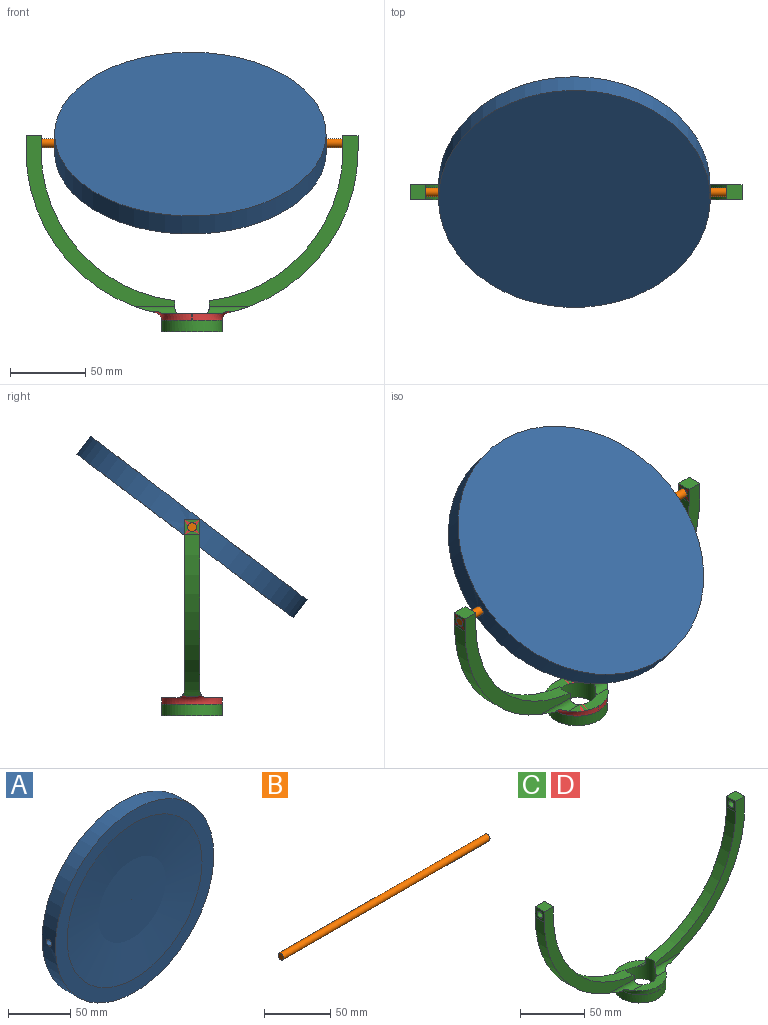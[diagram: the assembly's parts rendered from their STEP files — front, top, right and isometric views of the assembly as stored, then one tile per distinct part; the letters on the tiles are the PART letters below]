
ASSEMBLY  parts=4 mates=2
PART A: 5 faces, bbox 180x20.2x180 mm
  f0: cylinder r=90mm len=180mm, axis (0,1,0), area 8425mm2, adj f1,f2,f3
  f1: plane 180x180mm, normal (0,-1,0), area 7010.2mm2, adj f0,f4
  f2: plane 180x180mm, normal (0,1,0), area 25446.9mm2, adj f0
  f3: cylinder r=3mm len=180mm, axis (-1,0,0), area 3392mm2, adj f0
  f4: torus R=16.77mm, axis (0,1,0), area 18487.8mm2, adj f1
PART B: 3 faces, bbox 220x5.9x5.9 mm
  f0: cylinder r=2.95mm len=220mm, axis (-1,0,0), area 4077.8mm2, adj f1,f2
  f1: plane 5.9x5.9mm, normal (1,0,0), area 27.3mm2, adj f0
  f2: plane 5.9x5.9mm, normal (-1,0,0), area 27.3mm2, adj f0
PART C: 29 faces, bbox 220x40x130 mm
  f0: plane 113.17x98.54mm, normal (0,-1,0), area 1535.6mm2, adj f4,f5,f6,f12,f13,f21,f25
  f1: cylinder r=100mm len=99.34mm, axis (0,1,0), area 1448.9mm2, adj f3,f11,f14,f21
  f2: plane 113.17x98.54mm, normal (0,1,0), area 1535.6mm2, adj f4,f5,f6,f12,f13,f21,f23
  f3: plane 113.17x98.54mm, normal (0,-1,0), area 1535.6mm2, adj f1,f8,f9,f10,f11,f21,f22
  f4: plane 10x10mm, normal (0,0,1), area 100mm2, adj f0,f2,f5,f13
  f5: plane 10x10mm, normal (-1,0,0), area 71.7mm2, adj f0,f2,f4,f6,f15
  f6: cylinder r=110mm len=107.37mm, axis (0,1,0), area 1485.5mm2, adj f0,f2,f5,f23,f25,f26
  f7: plane 40x40mm, normal (0,0,-1), area 765.8mm2, adj f21,f27
  f8: cylinder r=110mm len=107.37mm, axis (0,1,0), area 1485.5mm2, adj f3,f9,f14,f22,f24,f28
  f9: plane 10x10mm, normal (1,0,0), area 71.7mm2, adj f3,f8,f10,f14,f16
  f10: plane 10x10mm, normal (0,0,1), area 100mm2, adj f3,f9,f11,f14
  f11: plane 10x10mm, normal (-1,0,0), area 71.7mm2, adj f1,f3,f10,f14,f16
  f12: cylinder r=100mm len=99.34mm, axis (0,1,0), area 1448.9mm2, adj f0,f2,f13,f21
  f13: plane 10x10mm, normal (1,0,0), area 71.7mm2, adj f0,f2,f4,f12,f15
  f14: plane 113.17x98.54mm, normal (0,1,0), area 1535.6mm2, adj f1,f8,f9,f10,f11,f21,f24
  f15: cylinder r=3mm len=10mm, axis (1,0,0), area 188.5mm2, adj f5,f13
  f16: cylinder r=3mm len=10mm, axis (1,0,0), area 188.5mm2, adj f9,f11
  f17: plane 36.99x10mm, normal (0,0,1), area 235.1mm2, adj f18,f21,f22,f25,f26,f28
  f18: plane 4.08x0.67mm, normal (0,-1,0), area 0.9mm2, adj f17,f26,f28
  f19: plane 36.99x10mm, normal (0,0,1), area 235.1mm2, adj f20,f21,f23,f24,f26,f28
  f20: plane 4.08x0.67mm, normal (0,1,0), area 0.9mm2, adj f19,f26,f28
  f21: cylinder r=12.5mm len=25mm, axis (0,0,-1), area 1136.4mm2, adj f0,f1,f2,f3,f7,f12,f14,f17
  f22: cylinder r=5mm len=30.67mm, axis (-1,0,0), area 123.8mm2, adj f3,f8,f17,f21,f28
  f23: cylinder r=5mm len=30.67mm, axis (-1,0,0), area 123.8mm2, adj f2,f6,f19,f21,f26
  f24: cylinder r=5mm len=30.67mm, axis (-1,0,0), area 123.8mm2, adj f8,f14,f19,f21,f28
  f25: cylinder r=5mm len=30.67mm, axis (-1,0,0), area 123.8mm2, adj f0,f6,f17,f21,f26
  f26: torus R=25mm, axis (0,-1,0), area 327.5mm2, adj f6,f17,f18,f19,f20,f23,f25,f27
  f27: cylinder r=20mm len=40mm, axis (0,0,1), area 973.9mm2, adj f7,f26,f28
  f28: torus R=25mm, axis (0,-1,0), area 327.5mm2, adj f8,f17,f18,f19,f20,f22,f24,f27
PART D: same geometry as C
PLACE A rot(axis=(1,0,0),127.1deg) t=(-6.37,-25.32,26.61)mm
PLACE B rot(axis=(-1,0,0),122.1deg) t=(-5.29,-25.32,26.61)mm
PLACE C t=(-5.29,-25.32,21.61)mm fixed
PLACE D t=(-5.29,-25.32,21.61)mm
MATE revolute C.f15 <-> B.f0  axis (1,0,0) through (104.71,-25.32,26.61)mm
MATE revolute A.f3 <-> B.f0  axis (-1,0,0) through (84.71,-25.32,26.61)mm
